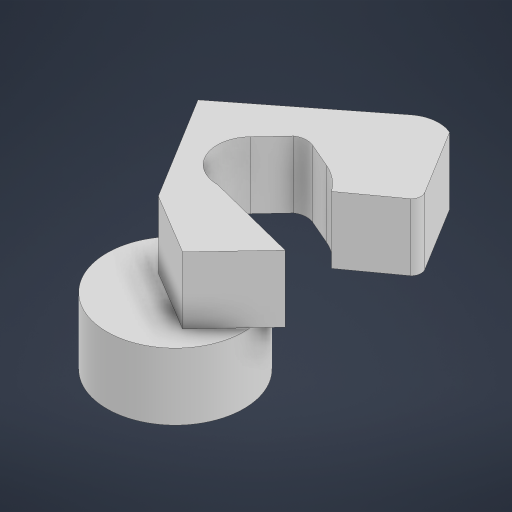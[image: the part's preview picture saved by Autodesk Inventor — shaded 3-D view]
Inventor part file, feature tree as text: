
AUTODESK INVENTOR PART (.ipt)
format: ipt  version: 2024.1 (Build 281209000, 209)  size: 196,608 bytes
history: native  units: in
note: dims shown in document units (in); Inventor stores cm internally (conversion verified against a paired STEP export)
features: extrude x2, sketch x2
ambient origin geometry x8: Origin, YZ Plane, XZ Plane, XY Plane, X Axis, Y Axis, Z Axis, Center Point
bodies: Solid1 (feature_tree)
feature tree (4):
  extrude  "Extrusion1"  Depth=1.0in TaperAngle=0.0deg
  extrude  "Extrusion2"  [1 undecoded]
  sketch  "Sketch1"  dims[d0=1.0in d1=0.0in d2=1.0in d3=0.0in]
  sketch  "Sketch2"
note: 1 required parameter value undecoded (feature->parameter linkage not recoverable at this tier; creation-order binding heuristic only, values carry confidence <= 0.55)
